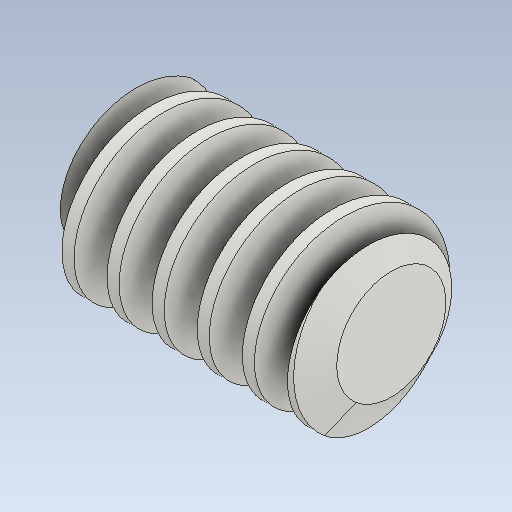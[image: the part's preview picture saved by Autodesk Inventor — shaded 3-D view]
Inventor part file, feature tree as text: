
AUTODESK INVENTOR PART (.ipt)
format: ipt  version: 2021 (Build 250183000, 183)  size: 359,424 bytes
history: native  units: mm (DEFAULTED — no unit token found)
features: other x6, chamfer x2, pattern_circular x2, extrude x1, sketch x1
ambient origin geometry x6: Origin, XZ Plane, X Axis, Y Axis, Z Axis, Center Point
bodies: Solid1 (feature_tree)
feature tree (12):
  extrude  "Base Body"  Depth=10.0mm
  chamfer  "Chamfer1"  Distance=38.1mm
  chamfer  "Chamfer2"  [1 undecoded]
  other  "Tooth Sketch"
  other  "Left Tooth"
  pattern_circular  "Left Tooth Pattern"  [2 undecoded]
  other  "Tooth"
  pattern_circular  "Tooth Pattern"  [2 undecoded]
  other  "Base Body Sketch"
  sketch  "Sketch5"  dims[d4=40.0mm d5=24.255213mm d6=38.1mm d7=0.0mm d8=1.618499mm d9=4.446789mm d10=1.618499mm d11=4.446789mm d12=19.198622mm d14=3.1425mm d24=19.198622mm d25=28.575mm d26=1.5875mm d27=7.680818mm d28=10.106339mm d29=12.248883mm d30=6.35mm d31=10.0mm d32=90.0mm d33=0.0mm d34=90.0deg d35=90.0deg d36=0.0mm d37=0.0mm d43=10.0mm d45=360.0deg d46=45.0deg d47=45.0deg d49=0.0mm d53=0.0mm d54=70.744372mm d55=0.0mm d56=0.0mm d57=20.212678mm d58=25.4mm d59=0.0mm d60=6.35mm d61=25.4mm d62=90.0mm d63=0.0mm d64=90.0deg d65=90.0deg d66=0.0mm d67=0.0mm d68=10.0mm d69=10.0mm d70=360.0deg d72=10.0mm d74=10.0mm d75=10.0mm d76=0.0mm d77=70.744372mm]
  other  "Srf1"
  other  "Pitch Diameter"
note: 5 required parameter values undecoded (feature->parameter linkage not recoverable at this tier; creation-order binding heuristic only, values carry confidence <= 0.55)
